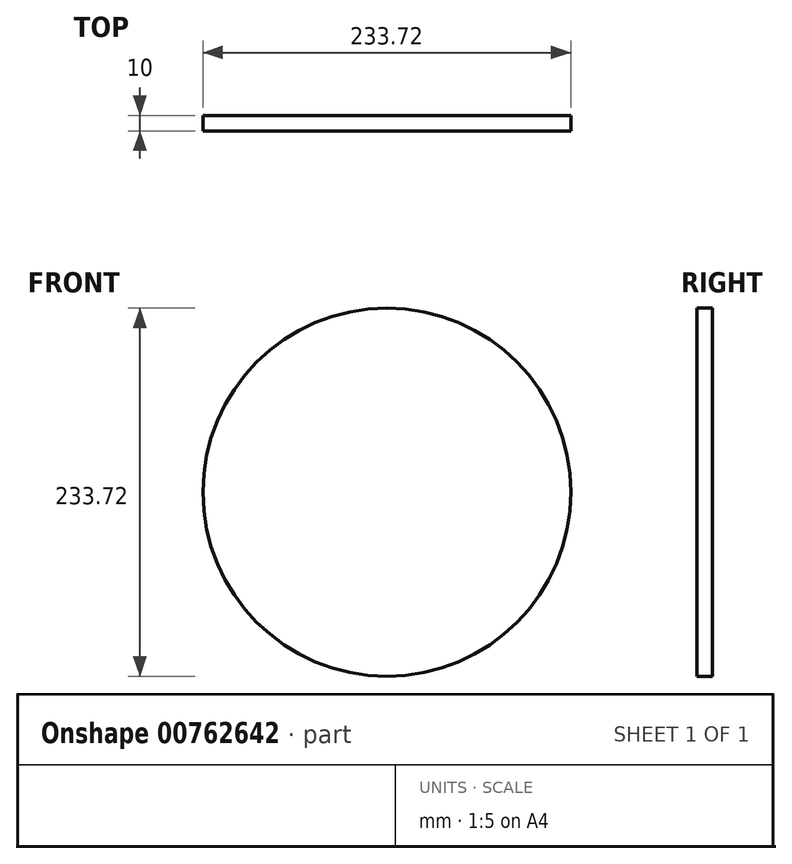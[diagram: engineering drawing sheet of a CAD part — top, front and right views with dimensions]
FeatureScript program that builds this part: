
annotation { "Feature Type Name" : "Feature", "Feature Type Description" : "" }
export const myFeature = defineFeature(function(context is Context, id is Id, definition is map)
    precondition{}
    {
        {
            var Q0;
            Q0=qCreatedBy(makeId("Front.planeOp"),FACE);
            var sketch = newSketch(context, id + "F0", { "sketchPlane" : qUnion([Q0])});
            skCircle(sketch, "E0", {"center": v(0, 0) * mm, "radius": 116.86 * mm});
            skSolve(sketch);
        }
        {
            var Q0;
            Q0 = qSketchRegion(id + "FWF1C0R07ymy2Yn_0", true);
            var Q1;
            Q1=sQuery(id+"F0.wireOp",EDGE,"E0");
            extrude(context, id + "F1", {"entities" : qUnion([Q0]), "bodyType" : ToolBodyType.SURFACE, "surfaceEntities" : qUnion([Q1]), "depth" : 10 * mm, "offsetDistance" : 25.4 * mm});
        }
    });
